# Revit family: КЛОП-2(90)–НО-МВ
name_source: partatom
category: Арматура воздуховодов
revit_build: Autodesk Revit 2016 (Build: 20161004_0715(x64)
units: mm (PartAtom-declared; Revit-internal decimal feet)

## family parameters
Всегда вертикально = Да
На основе рабочей плоскости = Нет
Общий = Нет
При загрузке вырезать с полостями = Нет
Размер круглого соединителя = Использовать радиус
Тип детали = Вставляется

## types (1)
- КЛОП-2(90)–НО-МВ
    ADSK_Единица измерения = шт
    ADSK_Завод-изготовитель = ВИНГС-М
    ADSK_Предел огнестойкости = EI90
    ADSK_Расход воздуха = 0.0 м³/ч
    P = 1.2000 кг/куб. м
    URL = https://www.vings-m.ru
    l = 330 мм
    l1 = 85 мм
    t_заслонки = 10 мм
    t_стенки = 5 мм
    ИСП01 = Простое исполнение
    ИСПА = Исполнение А
    ИСПБ = Исполнение Б
    Материал клапана = <По категории>
    Наличие соединительной коробки = Нет
    Таблица_выбора = КЛОП-2(90)–НО-МВ

## geometry (parser evidence)
native form markers: Blend x2
no freeform markers — native parametric forms only
